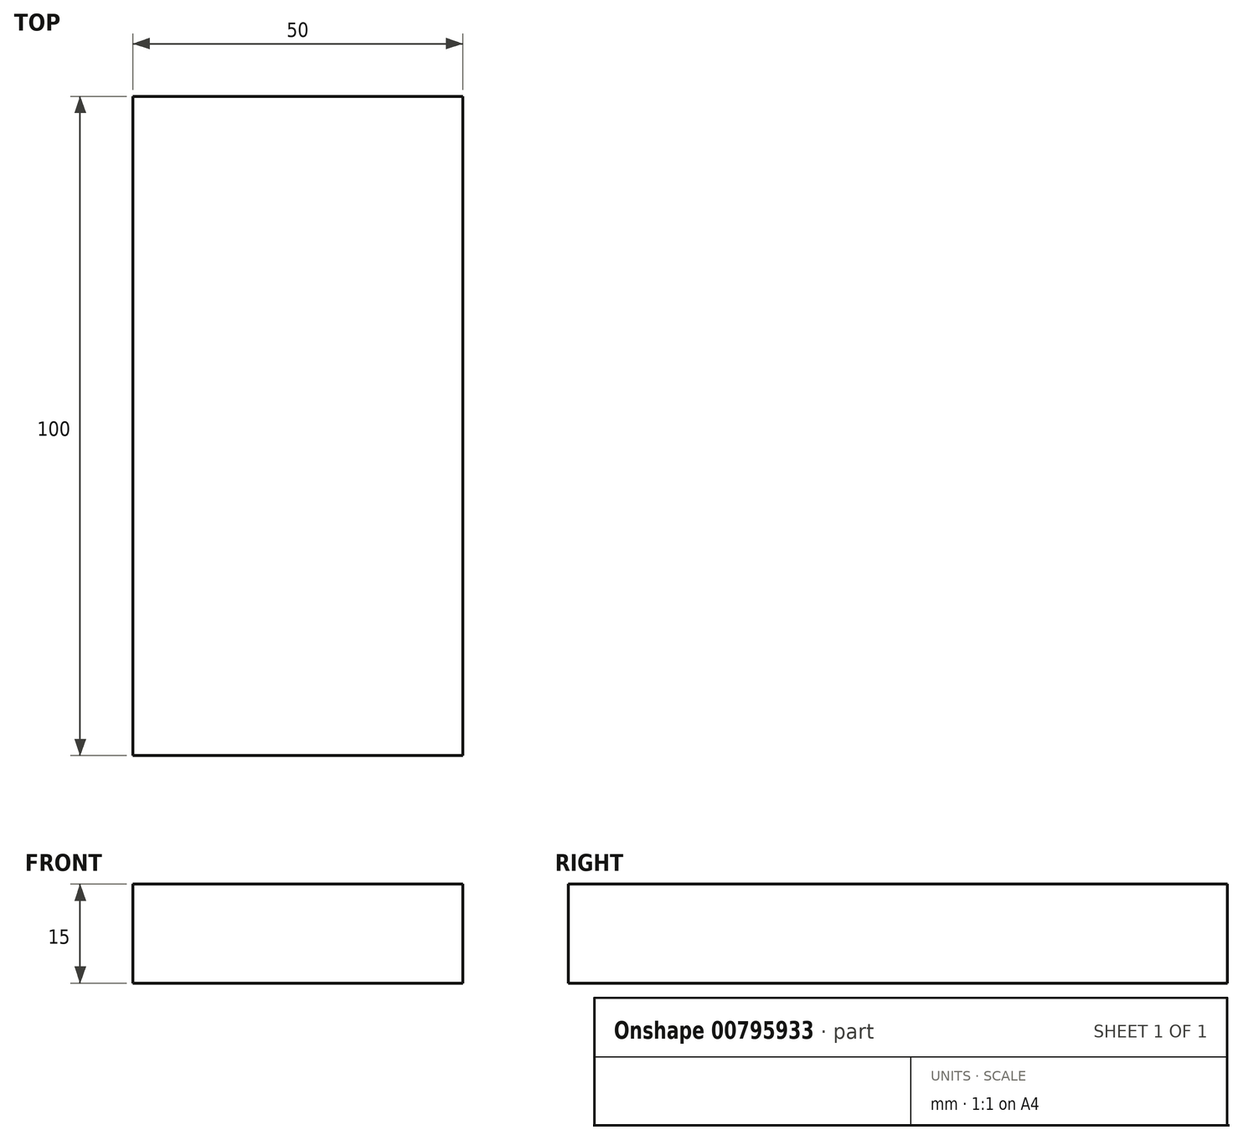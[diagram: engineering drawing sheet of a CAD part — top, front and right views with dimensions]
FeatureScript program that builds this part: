
annotation { "Feature Type Name" : "Feature", "Feature Type Description" : "" }
export const myFeature = defineFeature(function(context is Context, id is Id, definition is map)
    precondition{}
    {
        {
            var Q0;
            Q0=qCreatedBy(makeId("Top.planeOp"),FACE);
            var sketch = newSketch(context, id + "F0", { "sketchPlane" : qUnion([Q0])});
            skLineSegment(sketch, "E0.bottom", {"start": v(25, 50) * mm, "end": v(-25, 50) * mm});
            skLineSegment(sketch, "E0.top", {"start": v(25, -50) * mm, "end": v(-25, -50) * mm});
            skLineSegment(sketch, "E0.left", {"start": v(25, 50) * mm, "end": v(25, -50) * mm});
            skLineSegment(sketch, "E0.right", {"start": v(-25, 50) * mm, "end": v(-25, -50) * mm});
            skPoint(sketch, "E0.middle", {"position": v(0, 0) * mm});
            skSolve(sketch);
        }
        {
            var Q0;
            Q0 = qSketchRegion(id + "F0", true);
            extrude(context, id + "F1", {"entities" : qUnion([Q0]), "depth" : 15 * mm, "offsetDistance" : 25 * mm});
        }
    });
